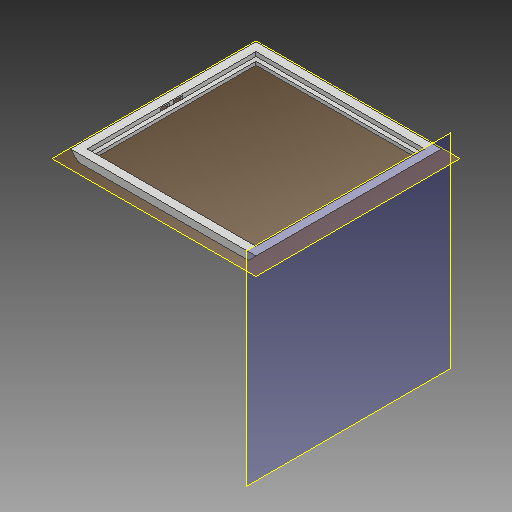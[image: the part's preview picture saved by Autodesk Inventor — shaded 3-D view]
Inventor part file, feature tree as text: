
AUTODESK INVENTOR PART (.ipt)
format: ipt  version: 2018.3 (Build 223284000, 284)  size: 206,336 bytes
history: native  units: mm
features: reference x20, other x12, extrude x6, sketch x6, plane x2, chamfer x1, projected_geometry x1
ambient origin geometry x8: Origin, YZ Plane, XZ Plane, XY Plane, X Axis, Y Axis, Z Axis, Center Point
bodies: Volumenkörper1 (feature_tree)
feature tree (48):
  extrude  "Extrusion1"  [1 undecoded]
  plane  "Arbeitsebene1"
  extrude  "Extrusion2"  Depth=10.0mm
  extrude  "Extrusion3"  Depth=10.0mm
  plane  "Arbeitsebene3"
  extrude  "Extrusion4"  Depth=8.0mm TaperAngle=0.0deg
  extrude  "Extrusion5"  Depth=2.0mm TaperAngle=0.0deg
  extrude  "Extrusion6"  Depth=18.0mm TaperAngle=45.0deg
  chamfer  "Fase2"  [1 undecoded]
  sketch  "Skizze1"  dims[d0=18.0mm d1=0.0mm d5=-20.0mm]
  reference  "Referenz1"
  reference  "Referenz2"
  reference  "Referenz3"
  reference  "Referenz4"
  reference  "Referenz5"
  sketch  "Skizze3"  dims[d6=17.0mm d7=0.0mm d8=10.0mm]
  reference  "Referenz12"
  reference  "Referenz13"
  reference  "Referenz14"
  reference  "Referenz15"
  reference  "Referenz16"
  reference  "Referenz17"
  reference  "Referenz18"
  reference  "Referenz19"
  sketch  "Skizze5"  dims[d9=10.0mm d10=10.0mm]
  sketch  "Skizze6"  dims[d11=10.0mm d12=8.0mm d13=0.0mm]
  reference  "Referenz20"
  reference  "Referenz21"
  reference  "Referenz22"
  reference  "Referenz23"
  reference  "Referenz24"
  reference  "Referenz25"
  sketch  "Skizze7"  dims[d14=25.0mm d15=0.0mm d16=2.0mm d17=0.0mm]
  projected_geometry  "Projizierte Kontur1"
  sketch  "Skizze8"  dims[d18=2.0mm d19=0.0mm d20=18.0mm d21=2.0mm d22=45.0deg]
  reference  "Referenz26"
  parser-record x2  (decoder bookkeeping rows leaked as tree rows — omitted from the tree; the rows remain in map.json)
  other  "SmartCube_Quadratisch.iam"
  other  "Wand2_MIR:1"
  other  "Wand1:1"
  other  "Wand1_MIR:1"
  other  "Wand2:1"
  other  "PV_Modul:1"
  other  "<userpath>\Documents\Dipl\Smartcube_Construction\Version_3\Baugruppe1.iam"
  other  "Baugruppe1.iam"
  other  "PV_Ramen_CPY_3_2:1"
  other  "PV_Modul_CPY_3_CPY1:1"
note: 2 required parameter values undecoded (feature->parameter linkage not recoverable at this tier; creation-order binding heuristic only, values carry confidence <= 0.55)
note: 2 file-system paths scrubbed to <path> (originals preserved in map.json)
